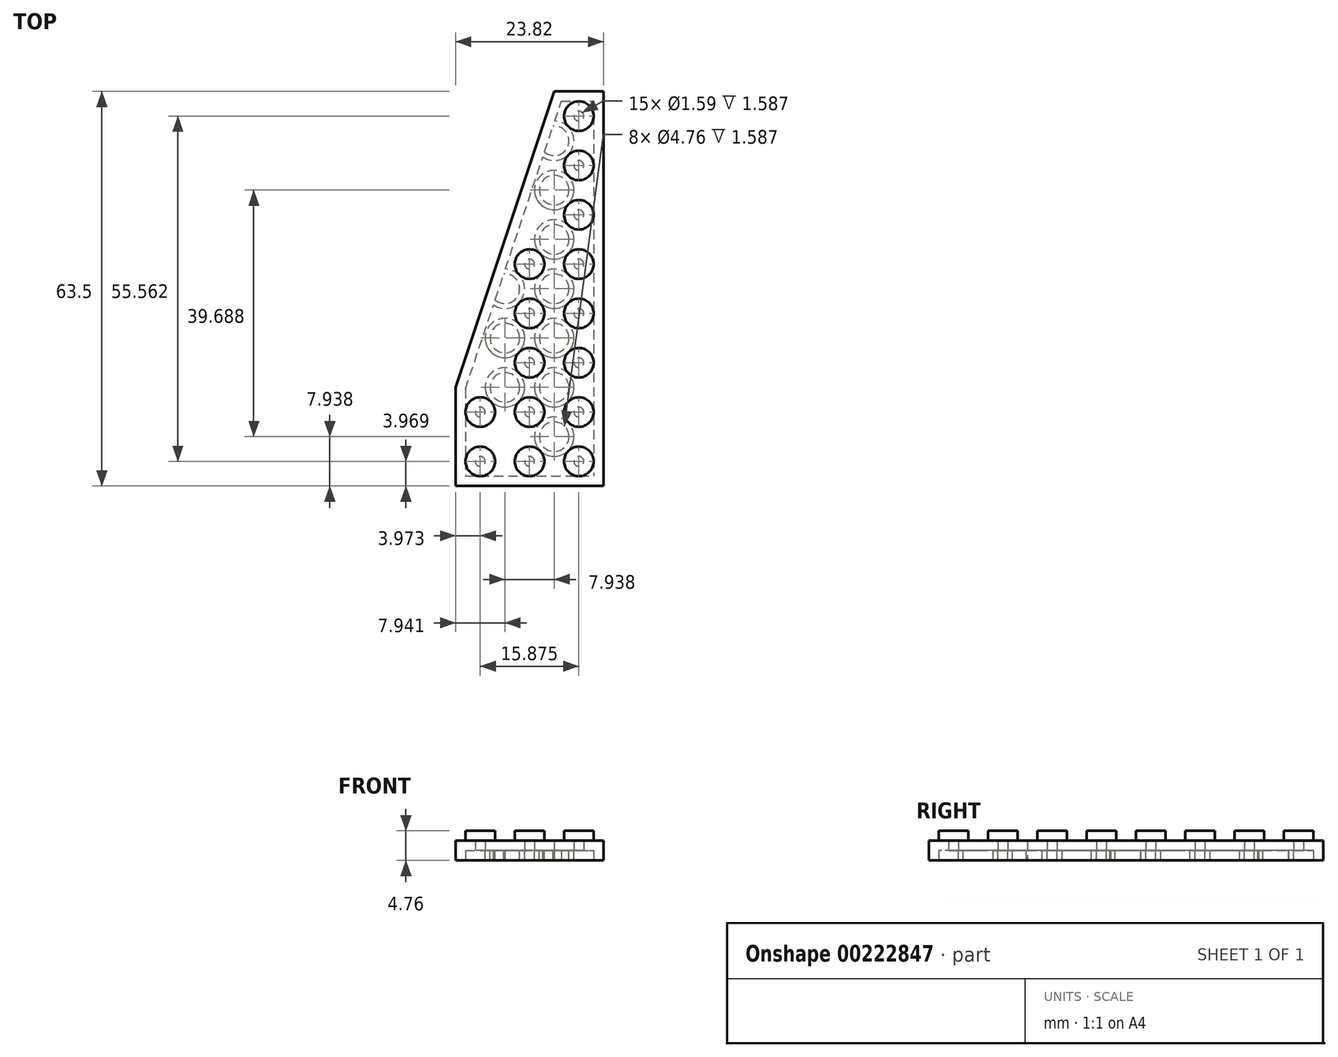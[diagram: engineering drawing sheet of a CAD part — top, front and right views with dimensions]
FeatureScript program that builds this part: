
annotation { "Feature Type Name" : "Feature", "Feature Type Description" : "" }
export const myFeature = defineFeature(function(context is Context, id is Id, definition is map)
    precondition{}
    {
        {
            var Q0;
            Q0=qCreatedBy(makeId("Top.planeOp"),FACE);
            var sketch = newSketch(context, id + "F0", { "sketchPlane" : qUnion([Q0])});
            skLineSegment(sketch, "E0.bottom", {"start": v(-11.9, 31.75) * mm, "end": v(11.9, 31.75) * mm});
            skLineSegment(sketch, "E0.top", {"start": v(-11.9, -31.75) * mm, "end": v(11.9, -31.75) * mm});
            skLineSegment(sketch, "E0.left", {"start": v(-11.9, 31.75) * mm, "end": v(-11.9, -31.75) * mm});
            skLineSegment(sketch, "E0.right", {"start": v(11.9, 31.75) * mm, "end": v(11.9, -31.75) * mm});
            skPoint(sketch, "E0.middle", {"position": v(0, 0) * mm});
            skPoint(sketch, "E1", {"position": v(3.97, 31.75) * mm});
            skPoint(sketch, "E2", {"position": v(-11.9, -15.87) * mm});
            skLineSegment(sketch, "E3", {"start": v(-11.9, -15.87) * mm, "end": v(3.97, 31.75) * mm});
            skCircle(sketch, "E4", {"center": v(7.94, -27.78) * mm, "radius": 2.38 * mm});
            skCircle(sketch, "E5.0.1.0", {"center": v(7.94, -19.84) * mm, "radius": 2.38 * mm});
            skCircle(sketch, "E5.1.0.0", {"center": v(0, -27.78) * mm, "radius": 2.38 * mm});
            skCircle(sketch, "E5.1.1.0", {"center": v(0, -19.84) * mm, "radius": 2.38 * mm});
            skCircle(sketch, "E5.2.0.0", {"center": v(-7.94, -27.78) * mm, "radius": 2.38 * mm});
            skCircle(sketch, "E5.2.1.0", {"center": v(-7.94, -19.84) * mm, "radius": 2.38 * mm});
            skLineSegment(sketch, "E5.direction1", {"start": v(7.94, -27.78) * mm, "end": v(0, -27.78) * mm, "construction": true});
            skLineSegment(sketch, "E5.direction2", {"start": v(7.94, -27.78) * mm, "end": v(7.94, -19.84) * mm, "construction": true});
            skCircle(sketch, "E6.0.1.0", {"center": v(7.94, -11.9) * mm, "radius": 2.38 * mm});
            skCircle(sketch, "E6.0.2.0", {"center": v(7.94, -3.97) * mm, "radius": 2.38 * mm});
            skCircle(sketch, "E6.0.3.0", {"center": v(7.94, 3.97) * mm, "radius": 2.38 * mm});
            skCircle(sketch, "E6.0.4.0", {"center": v(7.94, 11.9) * mm, "radius": 2.38 * mm});
            skCircle(sketch, "E6.0.5.0", {"center": v(7.94, 19.84) * mm, "radius": 2.38 * mm});
            skCircle(sketch, "E6.0.6.0", {"center": v(7.94, 27.78) * mm, "radius": 2.38 * mm});
            skLineSegment(sketch, "E6.direction1", {"start": v(7.94, -19.84) * mm, "end": v(33.34, -19.84) * mm, "construction": true});
            skLineSegment(sketch, "E6.direction2", {"start": v(7.94, -19.84) * mm, "end": v(7.94, -11.9) * mm, "construction": true});
            skCircle(sketch, "E7.0.1.0", {"center": v(0, -11.9) * mm, "radius": 2.38 * mm});
            skCircle(sketch, "E7.0.2.0", {"center": v(0, -3.97) * mm, "radius": 2.38 * mm});
            skCircle(sketch, "E7.0.3.0", {"center": v(0, 3.97) * mm, "radius": 2.38 * mm});
            skLineSegment(sketch, "E7.direction1", {"start": v(0, -19.84) * mm, "end": v(25.4, -19.84) * mm, "construction": true});
            skLineSegment(sketch, "E7.direction2", {"start": v(0, -19.84) * mm, "end": v(0, -11.9) * mm, "construction": true});
            skSolve(sketch);
        }
        {
            var Q0;
            {var subQ3=sQuery(id+"F0.wireOp",EDGE,"E0.top");Q0=makeQuery(id+"F0.imprint","IMPRINT",FACE,{"disambiguationData":[TD([[makeQuery(id+"F0.imprint","IMPRINT",EDGE,{"derivedFrom":subQ3}),1.0]])]});}
            extrude(context, id + "F1", {"entities" : qUnion([Q0]), "depth" : 3.17 * mm});
        }
        {
            var Q0;
            Q0=makeQuery(id+"F0.imprint","IMPRINT",FACE,{"disambiguationData":[TD([[makeQuery(id+"F0.imprint","IMPRINT",EDGE,{"derivedFrom":sQuery(id+"F0.wireOp",EDGE,"E6.0.6.0")}),1.0]])]});
            var Q1;
            Q1=makeQuery(id+"F0.imprint","IMPRINT",FACE,{"disambiguationData":[TD([[makeQuery(id+"F0.imprint","IMPRINT",EDGE,{"derivedFrom":sQuery(id+"F0.wireOp",EDGE,"E6.0.5.0")}),1.0]])]});
            var Q2;
            Q2=makeQuery(id+"F0.imprint","IMPRINT",FACE,{"disambiguationData":[TD([[makeQuery(id+"F0.imprint","IMPRINT",EDGE,{"derivedFrom":sQuery(id+"F0.wireOp",EDGE,"E6.0.4.0")}),1.0]])]});
            var Q3;
            Q3=makeQuery(id+"F0.imprint","IMPRINT",FACE,{"disambiguationData":[TD([[makeQuery(id+"F0.imprint","IMPRINT",EDGE,{"derivedFrom":sQuery(id+"F0.wireOp",EDGE,"E7.0.3.0")}),1.0]])]});
            var Q4;
            Q4=makeQuery(id+"F0.imprint","IMPRINT",FACE,{"disambiguationData":[TD([[makeQuery(id+"F0.imprint","IMPRINT",EDGE,{"derivedFrom":sQuery(id+"F0.wireOp",EDGE,"E6.0.3.0")}),1.0]])]});
            var Q5;
            Q5=makeQuery(id+"F0.imprint","IMPRINT",FACE,{"disambiguationData":[TD([[makeQuery(id+"F0.imprint","IMPRINT",EDGE,{"derivedFrom":sQuery(id+"F0.wireOp",EDGE,"E6.0.2.0")}),1.0]])]});
            var Q6;
            Q6=makeQuery(id+"F0.imprint","IMPRINT",FACE,{"disambiguationData":[TD([[makeQuery(id+"F0.imprint","IMPRINT",EDGE,{"derivedFrom":sQuery(id+"F0.wireOp",EDGE,"E7.0.2.0")}),1.0]])]});
            var Q7;
            Q7=makeQuery(id+"F0.imprint","IMPRINT",FACE,{"disambiguationData":[TD([[makeQuery(id+"F0.imprint","IMPRINT",EDGE,{"derivedFrom":sQuery(id+"F0.wireOp",EDGE,"E7.0.1.0")}),1.0]])]});
            var Q8;
            Q8=makeQuery(id+"F0.imprint","IMPRINT",FACE,{"disambiguationData":[TD([[makeQuery(id+"F0.imprint","IMPRINT",EDGE,{"derivedFrom":sQuery(id+"F0.wireOp",EDGE,"E6.0.1.0")}),1.0]])]});
            var Q9;
            Q9=makeQuery(id+"F0.imprint","IMPRINT",FACE,{"disambiguationData":[TD([[makeQuery(id+"F0.imprint","IMPRINT",EDGE,{"derivedFrom":sQuery(id+"F0.wireOp",EDGE,"E5.0.1.0")}),1.0]])]});
            var Q10;
            Q10=makeQuery(id+"F0.imprint","IMPRINT",FACE,{"disambiguationData":[TD([[makeQuery(id+"F0.imprint","IMPRINT",EDGE,{"derivedFrom":sQuery(id+"F0.wireOp",EDGE,"E5.1.1.0")}),1.0]])]});
            var Q11;
            Q11=makeQuery(id+"F0.imprint","IMPRINT",FACE,{"disambiguationData":[TD([[makeQuery(id+"F0.imprint","IMPRINT",EDGE,{"derivedFrom":sQuery(id+"F0.wireOp",EDGE,"E5.2.1.0")}),1.0]])]});
            var Q12;
            Q12=makeQuery(id+"F0.imprint","IMPRINT",FACE,{"disambiguationData":[TD([[makeQuery(id+"F0.imprint","IMPRINT",EDGE,{"derivedFrom":sQuery(id+"F0.wireOp",EDGE,"E5.2.0.0")}),1.0]])]});
            var Q13;
            Q13=makeQuery(id+"F0.imprint","IMPRINT",FACE,{"disambiguationData":[TD([[makeQuery(id+"F0.imprint","IMPRINT",EDGE,{"derivedFrom":sQuery(id+"F0.wireOp",EDGE,"E5.1.0.0")}),1.0]])]});
            var Q14;
            Q14=makeQuery(id+"F0.imprint","IMPRINT",FACE,{"disambiguationData":[TD([[makeQuery(id+"F0.imprint","IMPRINT",EDGE,{"derivedFrom":sQuery(id+"F0.wireOp",EDGE,"E4")}),1.0]])]});
            extrude(context, id + "F2", {"entities" : qUnion([Q0, Q1, Q2, Q3, Q4, Q5, Q6, Q7, Q8, Q9, Q10, Q11, Q12, Q13, Q14]), "operationType" : NewBodyOperationType.ADD, "depth" : 4.76 * mm});
        }
        {
            var Q0;
            {var subQ0=sQuery(id+"F0.wireOp",EDGE,"E7.0.3.0");var subQ1=sQuery(id+"F0.wireOp",EDGE,"E7.0.2.0");var subQ2=sQuery(id+"F0.wireOp",EDGE,"E7.0.1.0");var subQ3=sQuery(id+"F0.wireOp",EDGE,"E6.0.6.0");var subQ4=sQuery(id+"F0.wireOp",EDGE,"E6.0.5.0");var subQ5=sQuery(id+"F0.wireOp",EDGE,"E6.0.4.0");var subQ6=sQuery(id+"F0.wireOp",EDGE,"E6.0.3.0");var subQ7=sQuery(id+"F0.wireOp",EDGE,"E6.0.2.0");var subQ8=sQuery(id+"F0.wireOp",EDGE,"E6.0.1.0");var subQ9=sQuery(id+"F0.wireOp",EDGE,"E5.2.1.0");var subQ10=sQuery(id+"F0.wireOp",EDGE,"E5.2.0.0");var subQ11=sQuery(id+"F0.wireOp",EDGE,"E5.1.1.0");var subQ12=sQuery(id+"F0.wireOp",EDGE,"E5.1.0.0");var subQ13=sQuery(id+"F0.wireOp",EDGE,"E5.0.1.0");var subQ14=sQuery(id+"F0.wireOp",EDGE,"E4");Q0=makeQuery(id+"F2.boolean.opBoolean","MERGE",FACE,{"derivedFrom":[makeQuery(id+"F1.opExtrude","CAP_FACE",FACE,{"disambiguationData":[OSD([sQuery(id+"F0.wireOp",EDGE,"E0.bottom"),sQuery(id+"F0.wireOp",EDGE,"E0.top"),sQuery(id+"F0.wireOp",EDGE,"E0.left"),sQuery(id+"F0.wireOp",EDGE,"E0.right"),sQuery(id+"F0.wireOp",EDGE,"E3"),subQ14,subQ13,subQ12,subQ11,subQ10,subQ9,subQ8,subQ7,subQ6,subQ5,subQ4,subQ3,subQ2,subQ1,subQ0])],"isStart":true}),makeQuery(id+"F2.opExtrude","CAP_FACE",FACE,{"disambiguationData":[OSD([subQ14])],"isStart":true}),makeQuery(id+"F2.opExtrude","CAP_FACE",FACE,{"disambiguationData":[OSD([subQ13])],"isStart":true}),makeQuery(id+"F2.opExtrude","CAP_FACE",FACE,{"disambiguationData":[OSD([subQ12])],"isStart":true}),makeQuery(id+"F2.opExtrude","CAP_FACE",FACE,{"disambiguationData":[OSD([subQ11])],"isStart":true}),makeQuery(id+"F2.opExtrude","CAP_FACE",FACE,{"disambiguationData":[OSD([subQ10])],"isStart":true}),makeQuery(id+"F2.opExtrude","CAP_FACE",FACE,{"disambiguationData":[OSD([subQ9])],"isStart":true}),makeQuery(id+"F2.opExtrude","CAP_FACE",FACE,{"disambiguationData":[OSD([subQ8])],"isStart":true}),makeQuery(id+"F2.opExtrude","CAP_FACE",FACE,{"disambiguationData":[OSD([subQ7])],"isStart":true}),makeQuery(id+"F2.opExtrude","CAP_FACE",FACE,{"disambiguationData":[OSD([subQ6])],"isStart":true}),makeQuery(id+"F2.opExtrude","CAP_FACE",FACE,{"disambiguationData":[OSD([subQ5])],"isStart":true}),makeQuery(id+"F2.opExtrude","CAP_FACE",FACE,{"disambiguationData":[OSD([subQ4])],"isStart":true}),makeQuery(id+"F2.opExtrude","CAP_FACE",FACE,{"disambiguationData":[OSD([subQ3])],"isStart":true}),makeQuery(id+"F2.opExtrude","CAP_FACE",FACE,{"disambiguationData":[OSD([subQ2])],"isStart":true}),makeQuery(id+"F2.opExtrude","CAP_FACE",FACE,{"disambiguationData":[OSD([subQ1])],"isStart":true}),makeQuery(id+"F2.opExtrude","CAP_FACE",FACE,{"disambiguationData":[OSD([subQ0])],"isStart":true})]});}
            shell(context, id + "F3", {"entities" : qUnion([Q0]), "thickness" : 1.59 * mm});
        }
        {
            var Q0;
            Q0=makeQuery(id+"F3.opShell","OFFSET_FACE",FACE,{"disambiguationData":[OSD([sQuery(id+"F0.wireOp",EDGE,"E0.bottom"),sQuery(id+"F0.wireOp",EDGE,"E0.top"),sQuery(id+"F0.wireOp",EDGE,"E0.left"),sQuery(id+"F0.wireOp",EDGE,"E0.right"),sQuery(id+"F0.wireOp",EDGE,"E3"),sQuery(id+"F0.wireOp",EDGE,"E4"),sQuery(id+"F0.wireOp",EDGE,"E5.0.1.0"),sQuery(id+"F0.wireOp",EDGE,"E5.1.0.0"),sQuery(id+"F0.wireOp",EDGE,"E5.1.1.0"),sQuery(id+"F0.wireOp",EDGE,"E5.2.0.0"),sQuery(id+"F0.wireOp",EDGE,"E5.2.1.0"),sQuery(id+"F0.wireOp",EDGE,"E6.0.1.0"),sQuery(id+"F0.wireOp",EDGE,"E6.0.2.0"),sQuery(id+"F0.wireOp",EDGE,"E6.0.3.0"),sQuery(id+"F0.wireOp",EDGE,"E6.0.4.0"),sQuery(id+"F0.wireOp",EDGE,"E6.0.5.0"),sQuery(id+"F0.wireOp",EDGE,"E6.0.6.0"),sQuery(id+"F0.wireOp",EDGE,"E7.0.1.0"),sQuery(id+"F0.wireOp",EDGE,"E7.0.2.0"),sQuery(id+"F0.wireOp",EDGE,"E7.0.3.0")])]});
            var sketch = newSketch(context, id + "F4", { "sketchPlane" : qUnion([Q0])});
            skLineSegment(sketch, "E8", {"start": v(-7.94, 27.78) * mm, "end": v(0, 19.84) * mm});
            skCircle(sketch, "E9", {"center": v(-3.97, 23.81) * mm, "radius": 3.18 * mm});
            skCircle(sketch, "E10.0", {"center": v(-3.97, 23.81) * mm, "radius": 2.38 * mm});
            skCircle(sketch, "E11.0.1.0", {"center": v(-3.97, 15.87) * mm, "radius": 3.18 * mm});
            skCircle(sketch, "E11.0.1.1", {"center": v(-3.97, 15.87) * mm, "radius": 2.38 * mm});
            skCircle(sketch, "E11.0.2.0", {"center": v(-3.97, 7.94) * mm, "radius": 3.18 * mm});
            skCircle(sketch, "E11.0.2.1", {"center": v(-3.97, 7.94) * mm, "radius": 2.38 * mm});
            skCircle(sketch, "E11.0.3.0", {"center": v(-3.97, 0) * mm, "radius": 3.18 * mm});
            skCircle(sketch, "E11.0.3.1", {"center": v(-3.97, 0) * mm, "radius": 2.38 * mm});
            skCircle(sketch, "E11.0.4.0", {"center": v(-3.97, -7.94) * mm, "radius": 3.18 * mm});
            skCircle(sketch, "E11.0.4.1", {"center": v(-3.97, -7.94) * mm, "radius": 2.38 * mm});
            skCircle(sketch, "E11.0.5.0", {"center": v(-3.97, -15.88) * mm, "radius": 3.18 * mm});
            skCircle(sketch, "E11.0.5.1", {"center": v(-3.97, -15.88) * mm, "radius": 2.38 * mm});
            skCircle(sketch, "E11.0.6.0", {"center": v(-3.97, -23.81) * mm, "radius": 3.18 * mm});
            skCircle(sketch, "E11.0.6.1", {"center": v(-3.97, -23.81) * mm, "radius": 2.38 * mm});
            skCircle(sketch, "E11.1.0.0", {"center": v(3.97, 23.81) * mm, "radius": 3.18 * mm});
            skCircle(sketch, "E11.1.0.1", {"center": v(3.97, 23.81) * mm, "radius": 2.38 * mm});
            skCircle(sketch, "E11.1.1.0", {"center": v(3.97, 15.87) * mm, "radius": 3.18 * mm});
            skCircle(sketch, "E11.1.1.1", {"center": v(3.97, 15.87) * mm, "radius": 2.38 * mm});
            skCircle(sketch, "E11.1.2.0", {"center": v(3.97, 7.94) * mm, "radius": 3.18 * mm});
            skCircle(sketch, "E11.1.2.1", {"center": v(3.97, 7.94) * mm, "radius": 2.38 * mm});
            skCircle(sketch, "E11.1.3.0", {"center": v(3.97, 0) * mm, "radius": 3.18 * mm});
            skCircle(sketch, "E11.1.3.1", {"center": v(3.97, 0) * mm, "radius": 2.38 * mm});
            skCircle(sketch, "E11.1.4.0", {"center": v(3.97, -7.94) * mm, "radius": 3.18 * mm});
            skCircle(sketch, "E11.1.4.1", {"center": v(3.97, -7.94) * mm, "radius": 2.38 * mm});
            skCircle(sketch, "E11.1.5.0", {"center": v(3.97, -15.88) * mm, "radius": 3.18 * mm});
            skCircle(sketch, "E11.1.5.1", {"center": v(3.97, -15.88) * mm, "radius": 2.38 * mm});
            skCircle(sketch, "E11.1.6.0", {"center": v(3.97, -23.81) * mm, "radius": 3.18 * mm});
            skCircle(sketch, "E11.1.6.1", {"center": v(3.97, -23.81) * mm, "radius": 2.38 * mm});
            skLineSegment(sketch, "E11.direction1", {"start": v(-3.97, 23.81) * mm, "end": v(3.97, 23.81) * mm, "construction": true});
            skLineSegment(sketch, "E11.direction2", {"start": v(-3.97, 23.81) * mm, "end": v(-3.97, 15.87) * mm, "construction": true});
            skSolve(sketch);
        }
        {
            var Q0;
            {var subQ0=sQuery(id+"F4.wireOp",EDGE,"E9");var subQ1=sQuery(id+"F4.wireOp",EDGE,"E8");var subQ2=makeQuery(id+"F4.imprint","INTERSECT",VERTEX,{"disambiguationData":[OD(0.0)],"derivedFrom":[subQ1,subQ0]});Q0=makeQuery(id+"F4.imprint","IMPRINT",FACE,{"disambiguationData":[TD([[makeQuery(id+"F4.imprint","IMPRINT",EDGE,{"disambiguationData":[TD([[subQ2,-1.0]])],"derivedFrom":subQ1}),1.0]])]});}
            var Q1;
            {var subQ0=sQuery(id+"F4.wireOp",EDGE,"E9");var subQ1=sQuery(id+"F4.wireOp",EDGE,"E8");var subQ2=makeQuery(id+"F4.imprint","INTERSECT",VERTEX,{"disambiguationData":[OD(0.0)],"derivedFrom":[subQ1,subQ0]});Q1=makeQuery(id+"F4.imprint","IMPRINT",FACE,{"disambiguationData":[TD([[makeQuery(id+"F4.imprint","IMPRINT",EDGE,{"disambiguationData":[TD([[subQ2,-1.0]])],"derivedFrom":subQ1}),-1.0]])]});}
            var Q2;
            Q2=makeQuery(id+"F4.imprint","IMPRINT",FACE,{"disambiguationData":[TD([[makeQuery(id+"F4.imprint","IMPRINT",EDGE,{"derivedFrom":sQuery(id+"F4.wireOp",EDGE,"E11.1.0.0")}),1.0]])]});
            var Q3;
            Q3=makeQuery(id+"F4.imprint","IMPRINT",FACE,{"disambiguationData":[TD([[makeQuery(id+"F4.imprint","IMPRINT",EDGE,{"derivedFrom":sQuery(id+"F4.wireOp",EDGE,"E11.1.1.0")}),1.0]])]});
            var Q4;
            Q4=makeQuery(id+"F4.imprint","IMPRINT",FACE,{"disambiguationData":[TD([[makeQuery(id+"F4.imprint","IMPRINT",EDGE,{"derivedFrom":sQuery(id+"F4.wireOp",EDGE,"E11.0.1.0")}),1.0]])]});
            var Q5;
            Q5=makeQuery(id+"F4.imprint","IMPRINT",FACE,{"disambiguationData":[TD([[makeQuery(id+"F4.imprint","IMPRINT",EDGE,{"derivedFrom":sQuery(id+"F4.wireOp",EDGE,"E11.0.2.0")}),1.0]])]});
            var Q6;
            Q6=makeQuery(id+"F4.imprint","IMPRINT",FACE,{"disambiguationData":[TD([[makeQuery(id+"F4.imprint","IMPRINT",EDGE,{"derivedFrom":sQuery(id+"F4.wireOp",EDGE,"E11.1.2.0")}),1.0]])]});
            var Q7;
            {var subQ0=sQuery(id+"F4.wireOp",EDGE,"E11.0.3.0");var subQ1=sQuery(id+"F0.wireOp",EDGE,"E3");var subQ2=makeQuery(id+"F3.opShell","OFFSET_EDGE",EDGE,{"disambiguationData":[OSD([subQ1]),TDD([makeQuery(id+"F1.opExtrude","CAP_EDGE",EDGE,{"disambiguationData":[OSD([subQ1])],"isStart":false})])]});var subQ3=makeQuery(id+"F4.imprint","INTERSECT",VERTEX,{"disambiguationData":[OD(0.0)],"derivedFrom":[subQ2,subQ0]});Q7=makeQuery(id+"F4.imprint","IMPRINT",FACE,{"disambiguationData":[TD([[makeQuery(id+"F4.imprint","IMPRINT",EDGE,{"disambiguationData":[TD([[subQ3,1.0]])],"derivedFrom":subQ0}),1.0]])]});}
            var Q8;
            Q8=makeQuery(id+"F4.imprint","IMPRINT",FACE,{"disambiguationData":[TD([[makeQuery(id+"F4.imprint","IMPRINT",EDGE,{"derivedFrom":sQuery(id+"F4.wireOp",EDGE,"E11.1.4.0")}),1.0]])]});
            var Q9;
            Q9=makeQuery(id+"F4.imprint","IMPRINT",FACE,{"disambiguationData":[TD([[makeQuery(id+"F4.imprint","IMPRINT",EDGE,{"derivedFrom":sQuery(id+"F4.wireOp",EDGE,"E11.1.3.0")}),1.0]])]});
            var Q10;
            Q10=makeQuery(id+"F4.imprint","IMPRINT",FACE,{"disambiguationData":[TD([[makeQuery(id+"F4.imprint","IMPRINT",EDGE,{"derivedFrom":sQuery(id+"F4.wireOp",EDGE,"E11.1.5.0")}),1.0]])]});
            var Q11;
            {var subQ0=sQuery(id+"F4.wireOp",EDGE,"E11.1.6.0");var subQ1=sQuery(id+"F0.wireOp",EDGE,"E3");var subQ2=makeQuery(id+"F3.opShell","OFFSET_EDGE",EDGE,{"disambiguationData":[OSD([subQ1]),TDD([makeQuery(id+"F1.opExtrude","CAP_EDGE",EDGE,{"disambiguationData":[OSD([subQ1])],"isStart":false})])]});var subQ3=makeQuery(id+"F4.imprint","INTERSECT",VERTEX,{"disambiguationData":[OD(0.0)],"derivedFrom":[subQ2,subQ0]});Q11=makeQuery(id+"F4.imprint","IMPRINT",FACE,{"disambiguationData":[TD([[makeQuery(id+"F4.imprint","IMPRINT",EDGE,{"disambiguationData":[TD([[subQ3,-1.0]])],"derivedFrom":subQ0}),1.0]])]});}
            extrude(context, id + "F5", {"entities" : qUnion([Q0, Q1, Q2, Q3, Q4, Q5, Q6, Q7, Q8, Q9, Q10, Q11]), "operationType" : NewBodyOperationType.ADD, "depth" : 1.59 * mm});
        }
    });
